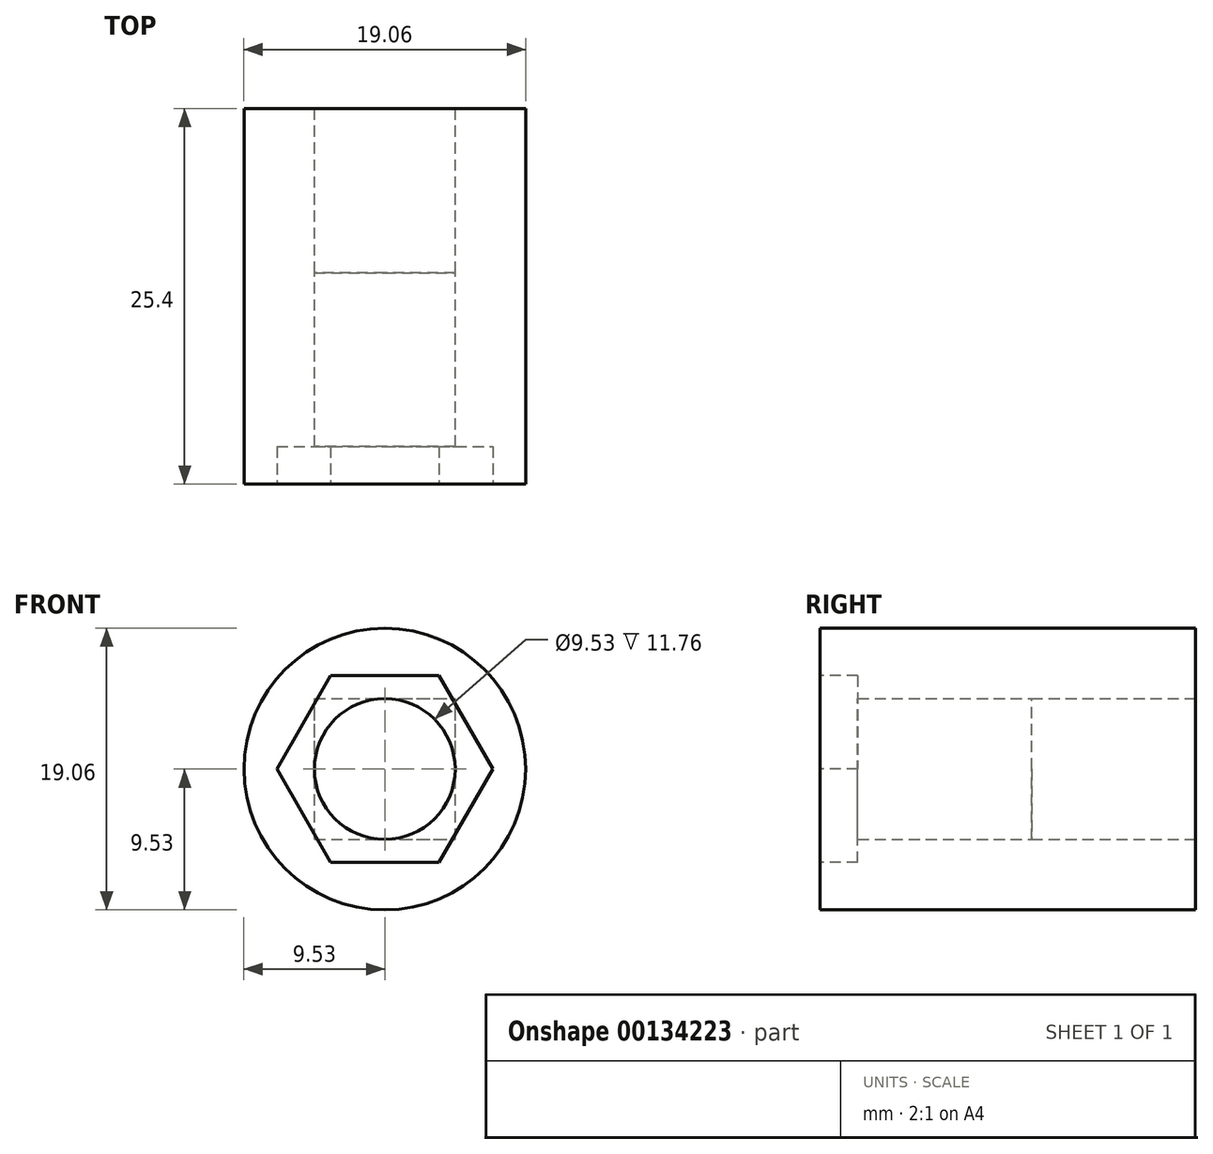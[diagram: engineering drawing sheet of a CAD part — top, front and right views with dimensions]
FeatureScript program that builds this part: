
annotation { "Feature Type Name" : "Feature", "Feature Type Description" : "" }
export const myFeature = defineFeature(function(context is Context, id is Id, definition is map)
    precondition{}
    {
        {
            var Q0;
            Q0=qCreatedBy(makeId("Front.planeOp"),FACE);
            var sketch = newSketch(context, id + "F0", { "sketchPlane" : qUnion([Q0])});
            skCircle(sketch, "E0", {"center": v(0, 0) * mm, "radius": 9.53 * mm});
            skSolve(sketch);
        }
        {
            var Q0;
            Q0 = qSketchRegion(id + "F0", true);
            extrude(context, id + "F1", {"entities" : qUnion([Q0]), "depth" : 25.4 * mm});
        }
        {
            var Q0;
            Q0=qCreatedBy(makeId("Front.planeOp"),FACE);
            var sketch = newSketch(context, id + "F2", { "sketchPlane" : qUnion([Q0])});
            skLineSegment(sketch, "E1.bottom", {"start": v(-4.76, -4.76) * mm, "end": v(4.76, -4.76) * mm});
            skLineSegment(sketch, "E1.top", {"start": v(-4.76, 4.76) * mm, "end": v(4.76, 4.76) * mm});
            skLineSegment(sketch, "E1.left", {"start": v(-4.76, -4.76) * mm, "end": v(-4.76, 4.76) * mm});
            skLineSegment(sketch, "E1.right", {"start": v(4.76, -4.76) * mm, "end": v(4.76, 4.76) * mm});
            skCircle(sketch, "E2", {"center": v(0, 0) * mm, "radius": 4.76 * mm});
            skSolve(sketch);
        }
        {
            var Q0;
            {var subQ0=sQuery(id+"F2.wireOp",EDGE,"E2");var subQ1=makeQuery(id+"F2.imprint","INTERSECT",VERTEX,{"derivedFrom":[sQuery(id+"F2.wireOp",EDGE,"E1.top"),subQ0]});Q0=makeQuery(id+"F2.imprint","IMPRINT",FACE,{"disambiguationData":[TD([[makeQuery(id+"F2.imprint","IMPRINT",EDGE,{"disambiguationData":[TD([[subQ1,1.0]])],"derivedFrom":subQ0}),1.0]])]});}
            extrude(context, id + "F3", {"entities" : qUnion([Q0]), "operationType" : NewBodyOperationType.REMOVE, "depth" : 25.4 * mm});
        }
        {
            var Q0;
            Q0 = qSketchRegion(id + "F2", true);
            extrude(context, id + "F4", {"entities" : qUnion([Q0]), "operationType" : NewBodyOperationType.REMOVE, "depth" : 11.1 * mm});
        }
        {
            var Q0;
            Q0=makeQuery(id+"F1.opExtrude","CAP_FACE",FACE,{"disambiguationData":[OSD([sQuery(id+"F0.wireOp",EDGE,"E0")])],"isStart":false});
            var sketch = newSketch(context, id + "F5", { "sketchPlane" : qUnion([Q0])});
            skCircle(sketch, "E3.cCircle", {"center": v(0, 0) * mm, "radius": 6.32 * mm, "construction": true});
            skLineSegment(sketch, "E3.0", {"start": v(3.65, 6.32) * mm, "end": v(7.3, 0) * mm});
            skLineSegment(sketch, "E3.1", {"start": v(7.3, 0) * mm, "end": v(3.65, -6.32) * mm});
            skLineSegment(sketch, "E3.2", {"start": v(3.65, -6.32) * mm, "end": v(-3.65, -6.32) * mm});
            skLineSegment(sketch, "E3.3", {"start": v(-3.65, -6.32) * mm, "end": v(-7.3, 0) * mm});
            skLineSegment(sketch, "E3.4", {"start": v(-7.3, 0) * mm, "end": v(-3.65, 6.32) * mm});
            skLineSegment(sketch, "E3.5", {"start": v(-3.65, 6.32) * mm, "end": v(3.65, 6.32) * mm});
            skPoint(sketch, "E3.0.midPoint", {"position": v(5.48, 3.16) * mm});
            skSolve(sketch);
        }
        {
            var Q0;
            Q0 = qSketchRegion(id + "F5", true);
            extrude(context, id + "F6", {"entities" : qUnion([Q0]), "operationType" : NewBodyOperationType.REMOVE, "oppositeDirection" : true, "depth" : 2.54 * mm});
        }
    });
